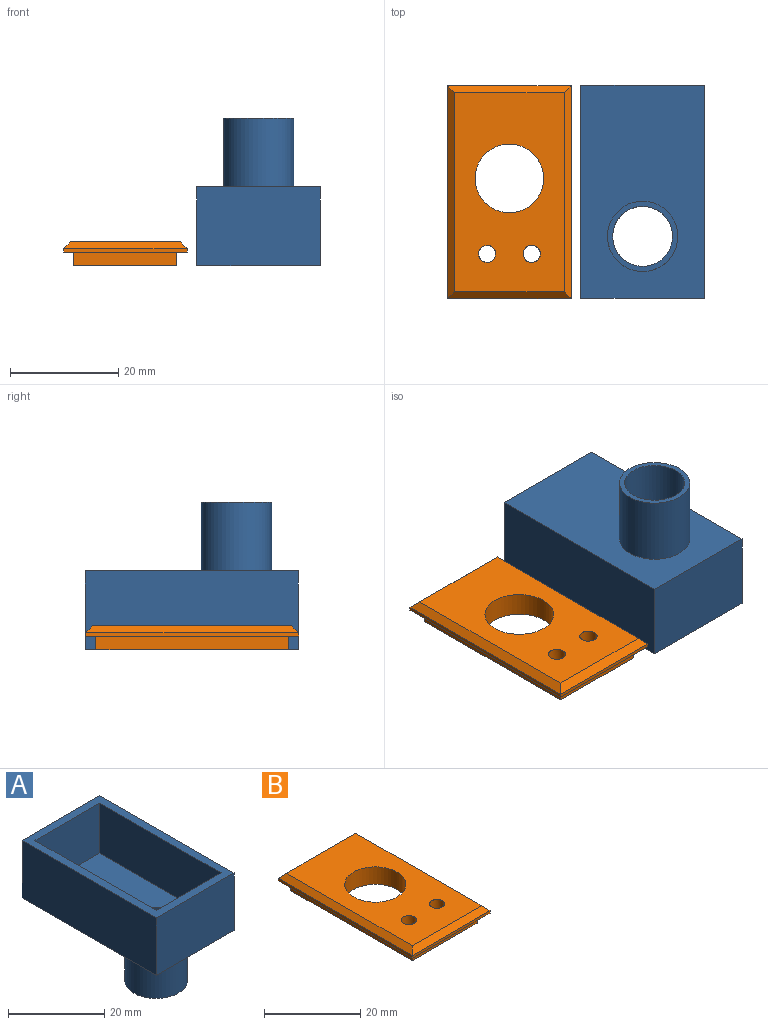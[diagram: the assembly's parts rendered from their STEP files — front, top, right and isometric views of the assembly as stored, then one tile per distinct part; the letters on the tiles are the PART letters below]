
ASSEMBLY  parts=2 mates=1
PART A: 14 faces, bbox 22.9x39.4x27.3 mm
  f0: plane 22.86x14.61mm, normal (0,1,0), area 333.9mm2, adj f1,f3,f4,f9
  f1: plane 39.37x14.61mm, normal (-1,0,0), area 575mm2, adj f0,f2,f4,f9
  f2: plane 22.86x14.61mm, normal (0,-1,0), area 333.9mm2, adj f1,f3,f4,f9
  f3: plane 39.37x14.61mm, normal (1,0,0), area 575mm2, adj f0,f2,f4,f9
  f4: plane 39.37x22.86mm, normal (0,0,-1), area 767.3mm2, adj f0,f1,f2,f3,f11
  f5: plane 35.56x12.7mm, normal (1,0,0), area 451.6mm2, adj f6,f8,f9,f10
  f6: plane 19.05x12.7mm, normal (0,-1,0), area 241.9mm2, adj f5,f7,f9,f10
  f7: plane 35.56x12.7mm, normal (-1,0,0), area 451.6mm2, adj f6,f8,f9,f10
  f8: plane 19.05x12.7mm, normal (0,1,0), area 241.9mm2, adj f5,f7,f9,f10
  f9: plane 39.37x22.86mm, normal (0,0,1), area 222.6mm2, adj f0,f1,f2,f3,f5,f6,f7,f8
  f10: plane 35.56x19.05mm, normal (0,0,1), area 580.7mm2, adj f5,f6,f7,f8,f13
  f11: cylinder r=6.5mm len=13mm, axis (0,0,1), area 518.7mm2, adj f4,f12
  f12: plane 13x13mm, normal (0,0,-1), area 36.1mm2, adj f11,f13
  f13: cylinder r=5.55mm len=14.61mm, axis (0,0,-1), area 509.1mm2, adj f10,f12
PART B: 22 faces, bbox 22.9x39.4x4.4 mm
  f0: cylinder r=1.59mm len=3.18mm, axis (0,0,-1), area 25.3mm2, adj f7,f21
  f1: cylinder r=1.59mm len=3.18mm, axis (0,0,-1), area 25.3mm2, adj f7,f18
  f2: plane 22.86x0.64mm, normal (0,1,0), area 14.5mm2, adj f3,f6,f8,f12
  f3: plane 39.37x0.64mm, normal (-1,0,0), area 25mm2, adj f2,f4,f8,f10
  f4: plane 22.86x0.64mm, normal (0,-1,0), area 14.5mm2, adj f3,f6,f8,f9
  f5: cylinder r=6.35mm len=12.7mm, axis (0,0,-1), area 177.3mm2, adj f7,f17
  f6: plane 39.37x0.64mm, normal (1,0,0), area 25mm2, adj f2,f4,f8,f11
  f7: plane 36.83x20.32mm, normal (0,0,1), area 605.9mm2, adj f0,f1,f5,f9,f10,f11,f12
  f8: plane 39.37x22.86mm, normal (0,0,-1), area 222.6mm2, adj f2,f3,f4,f6,f13,f14,f15,f16
  f9: plane 22.86x1.27mm, normal (0,-0.71,0.71), area 38.8mm2, adj f4,f7,f10,f11
  f10: plane 39.37x1.27mm, normal (-0.71,0,0.71), area 68.4mm2, adj f3,f7,f9,f12
  f11: plane 39.37x1.27mm, normal (0.71,0,0.71), area 68.4mm2, adj f6,f7,f9,f12
  f12: plane 22.86x1.27mm, normal (0,0.71,0.71), area 38.8mm2, adj f2,f7,f10,f11
  f13: plane 19.05x2.54mm, normal (0,-1,0), area 48.4mm2, adj f8,f14,f16,f17
  f14: plane 35.56x2.54mm, normal (-1,0,0), area 90.3mm2, adj f8,f13,f15,f17
  f15: plane 19.05x2.54mm, normal (0,1,0), area 48.4mm2, adj f8,f14,f16,f17
  f16: plane 35.56x2.54mm, normal (1,0,0), area 90.3mm2, adj f8,f13,f15,f17
  f17: plane 35.56x19.05mm, normal (0,0,-1), area 519.7mm2, adj f5,f13,f14,f15,f16,f19,f20
  f18: plane 4.45x4.45mm, normal (0,0,-1), area 7.6mm2, adj f1,f19
  f19: cylinder r=2.22mm len=4.45mm, axis (0,0,-1), area 26.6mm2, adj f17,f18
  f20: cylinder r=2.22mm len=4.45mm, axis (0,0,-1), area 26.6mm2, adj f17,f21
  f21: plane 4.45x4.45mm, normal (0,0,-1), area 7.6mm2, adj f0,f20
PLACE A rot(axis=(0,1,0),180deg) t=(12.31,-2.19,12.7)mm
PLACE B t=(-12.34,-2.24,-10.16)mm
MATE planar A.f9 <-> B.f17  axis (0,0,-1) through (12.31,-2.19,0)mm
